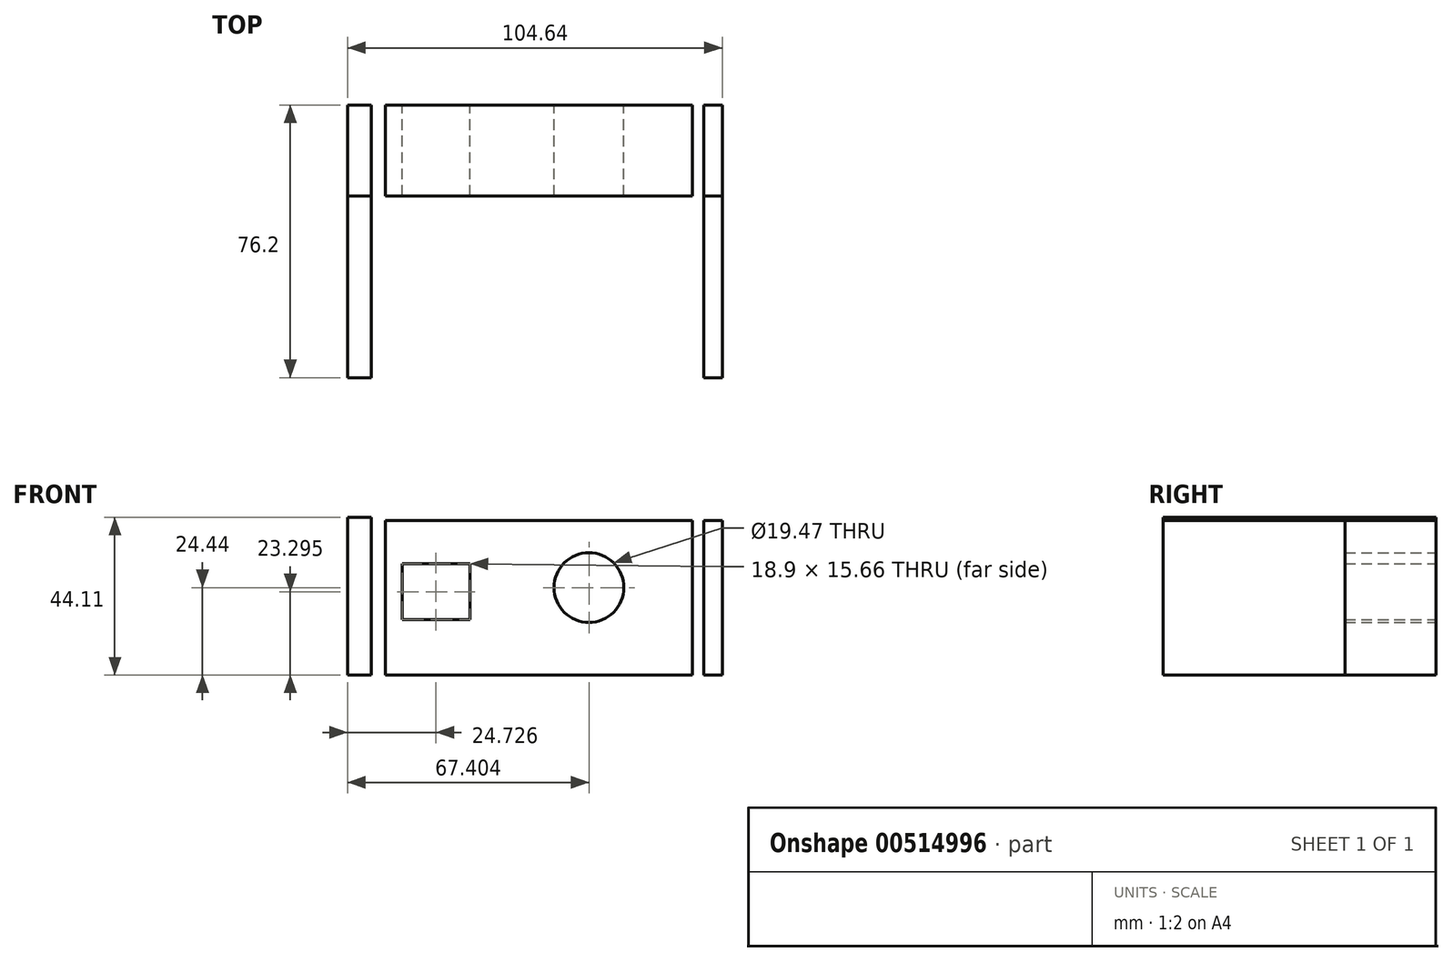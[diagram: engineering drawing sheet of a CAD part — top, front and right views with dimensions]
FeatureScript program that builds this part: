
annotation { "Feature Type Name" : "Feature", "Feature Type Description" : "" }
export const myFeature = defineFeature(function(context is Context, id is Id, definition is map)
    precondition{}
    {
        {
            var Q0;
            Q0=qCreatedBy(makeId("Front.planeOp"),FACE);
            var sketch = newSketch(context, id + "F0", { "sketchPlane" : qUnion([Q0])});
            skLineSegment(sketch, "E0.bottom", {"start": v(-44.11, 38.76) * mm, "end": v(41.63, 38.76) * mm});
            skLineSegment(sketch, "E0.top", {"start": v(-44.11, -4.4) * mm, "end": v(41.63, -4.4) * mm});
            skLineSegment(sketch, "E0.left", {"start": v(-44.11, 38.76) * mm, "end": v(-44.11, -4.4) * mm});
            skLineSegment(sketch, "E0.right", {"start": v(41.63, 38.76) * mm, "end": v(41.63, -4.4) * mm});
            skLineSegment(sketch, "E1.bottom", {"start": v(-47.93, 39.72) * mm, "end": v(-54.61, 39.72) * mm});
            skLineSegment(sketch, "E1.top", {"start": v(-47.93, -4.4) * mm, "end": v(-54.61, -4.4) * mm});
            skLineSegment(sketch, "E1.left", {"start": v(-47.93, 39.72) * mm, "end": v(-47.93, -4.4) * mm});
            skLineSegment(sketch, "E1.right", {"start": v(-54.61, 39.72) * mm, "end": v(-54.61, -4.4) * mm});
            skLineSegment(sketch, "E2.bottom", {"start": v(44.87, 38.76) * mm, "end": v(50.03, 38.76) * mm});
            skLineSegment(sketch, "E2.top", {"start": v(44.87, -4.4) * mm, "end": v(50.03, -4.4) * mm});
            skLineSegment(sketch, "E2.left", {"start": v(44.87, 38.76) * mm, "end": v(44.87, -4.4) * mm});
            skLineSegment(sketch, "E2.right", {"start": v(50.03, 38.76) * mm, "end": v(50.03, -4.4) * mm});
            skCircle(sketch, "E3", {"center": v(12.8, 20.05) * mm, "radius": 9.74 * mm});
            skLineSegment(sketch, "E4.bottom", {"start": v(-39.34, 26.73) * mm, "end": v(-20.43, 26.73) * mm});
            skLineSegment(sketch, "E4.top", {"start": v(-39.34, 11.08) * mm, "end": v(-20.43, 11.08) * mm});
            skLineSegment(sketch, "E4.left", {"start": v(-39.34, 26.73) * mm, "end": v(-39.34, 11.08) * mm});
            skLineSegment(sketch, "E4.right", {"start": v(-20.43, 26.73) * mm, "end": v(-20.43, 11.08) * mm});
            skSolve(sketch);
        }
        {
            var Q0;
            Q0=makeQuery(id+"F0.imprint","IMPRINT",FACE,{"disambiguationData":[TD([[makeQuery(id+"F0.imprint","IMPRINT",EDGE,{"derivedFrom":sQuery(id+"F0.wireOp",EDGE,"E1.bottom")}),1.0]])]});
            var Q1;
            Q1=makeQuery(id+"F0.imprint","IMPRINT",FACE,{"disambiguationData":[TD([[makeQuery(id+"F0.imprint","IMPRINT",EDGE,{"derivedFrom":sQuery(id+"F0.wireOp",EDGE,"E2.bottom")}),-1.0]])]});
            var Q2;
            Q2=makeQuery(id+"F0.imprint","IMPRINT",FACE,{"disambiguationData":[TD([[makeQuery(id+"F0.imprint","IMPRINT",EDGE,{"derivedFrom":sQuery(id+"F0.wireOp",EDGE,"E0.bottom")}),-1.0]])]});
            extrude(context, id + "F1", {"entities" : qUnion([Q0, Q1, Q2]), "depth" : 25.4 * mm, "offsetDistance" : 25.4 * mm});
        }
        {
            var Q0;
            Q0=makeQuery(id+"F1.opExtrude","CAP_FACE",FACE,{"disambiguationData":[OSD([sQuery(id+"F0.wireOp",EDGE,"E2.bottom"),sQuery(id+"F0.wireOp",EDGE,"E2.top"),sQuery(id+"F0.wireOp",EDGE,"E2.left"),sQuery(id+"F0.wireOp",EDGE,"E2.right")])],"isStart":false});
            var Q1;
            Q1=makeQuery(id+"F1.opExtrude","CAP_FACE",FACE,{"disambiguationData":[OSD([sQuery(id+"F0.wireOp",EDGE,"E1.bottom"),sQuery(id+"F0.wireOp",EDGE,"E1.top"),sQuery(id+"F0.wireOp",EDGE,"E1.left"),sQuery(id+"F0.wireOp",EDGE,"E1.right")])],"isStart":false});
            extrude(context, id + "F2", {"entities" : qUnion([Q0, Q1]), "depth" : 50.8 * mm, "offsetDistance" : 25.4 * mm});
        }
    });
